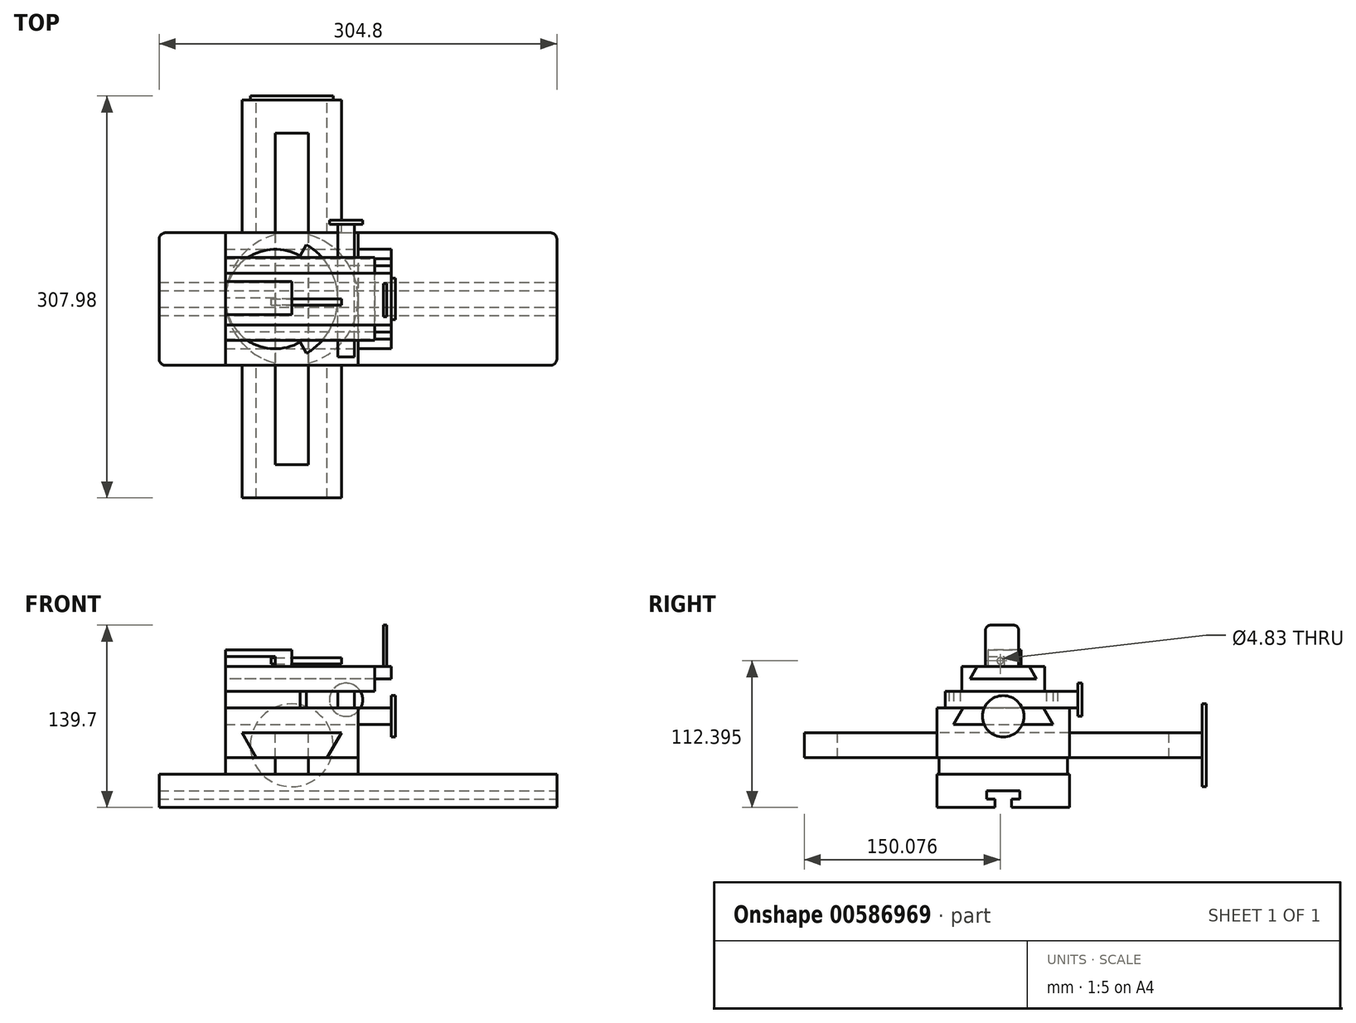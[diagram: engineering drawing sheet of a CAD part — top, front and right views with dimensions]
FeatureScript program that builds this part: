
annotation { "Feature Type Name" : "Feature", "Feature Type Description" : "" }
export const myFeature = defineFeature(function(context is Context, id is Id, definition is map)
    precondition{}
    {
        {
            var Q0;
            Q0=qCreatedBy(makeId("Top.planeOp"),FACE);
            var sketch = newSketch(context, id + "F0", { "sketchPlane" : qUnion([Q0])});
            skLineSegment(sketch, "E0.bottom", {"start": v(0, 0) * mm, "end": v(304.8, 0) * mm});
            skLineSegment(sketch, "E0.top", {"start": v(0, 101.6) * mm, "end": v(304.8, 101.6) * mm});
            skLineSegment(sketch, "E0.left", {"start": v(0, 0) * mm, "end": v(0, 101.6) * mm});
            skLineSegment(sketch, "E0.right", {"start": v(304.8, 0) * mm, "end": v(304.8, 101.6) * mm});
            skSolve(sketch);
        }
        {
            var Q0;
            Q0 = qSketchRegion(id + "F0", true);
            extrude(context, id + "F1", {"entities" : qUnion([Q0]), "depth" : 25.4 * mm, "offsetDistance" : 25.4 * mm});
        }
        {
            var Q0;
            Q0=makeQuery(id+"F1.opExtrude","SWEPT_EDGE",EDGE,{"disambiguationData":[OSD([sQuery(id+"F0.wireOp",EDGE,"E0.bottom"),sQuery(id+"F0.wireOp",EDGE,"E0.left")])]});
            var Q1;
            Q1=makeQuery(id+"F1.opExtrude","SWEPT_EDGE",EDGE,{"disambiguationData":[OSD([sQuery(id+"F0.wireOp",EDGE,"E0.bottom"),sQuery(id+"F0.wireOp",EDGE,"E0.right")])]});
            var Q2;
            Q2=makeQuery(id+"F1.opExtrude","SWEPT_EDGE",EDGE,{"disambiguationData":[OSD([sQuery(id+"F0.wireOp",EDGE,"E0.top"),sQuery(id+"F0.wireOp",EDGE,"E0.right")])]});
            var Q3;
            Q3=makeQuery(id+"F1.opExtrude","SWEPT_EDGE",EDGE,{"disambiguationData":[OSD([sQuery(id+"F0.wireOp",EDGE,"E0.top"),sQuery(id+"F0.wireOp",EDGE,"E0.left")])]});
            fillet(context, id + "F2", {"entities" : qUnion([Q0, Q1, Q2, Q3]), "radius" : 5.08 * mm, "tangentPropagation" : true, "allowEdgeOverflow" : false});
        }
        {
            var Q0;
            Q0=makeQuery(id+"F1.opExtrude","SWEPT_FACE",FACE,{"disambiguationData":[OSD([sQuery(id+"F0.wireOp",EDGE,"E0.right")])]});
            var sketch = newSketch(context, id + "F3", { "sketchPlane" : qUnion([Q0])});
            skLineSegment(sketch, "E1", {"start": v(44.45, 0) * mm, "end": v(44.45, 6.35) * mm});
            skLineSegment(sketch, "E2", {"start": v(44.45, 6.35) * mm, "end": v(38.1, 6.35) * mm});
            skLineSegment(sketch, "E3", {"start": v(38.1, 6.35) * mm, "end": v(38.1, 12.7) * mm});
            skLineSegment(sketch, "E4", {"start": v(38.1, 12.7) * mm, "end": v(63.5, 12.7) * mm});
            skLineSegment(sketch, "E5", {"start": v(63.5, 12.7) * mm, "end": v(63.5, 6.35) * mm});
            skLineSegment(sketch, "E6", {"start": v(63.5, 6.35) * mm, "end": v(57.15, 6.35) * mm});
            skLineSegment(sketch, "E7", {"start": v(57.15, 6.35) * mm, "end": v(57.15, 0) * mm});
            skLineSegment(sketch, "E8", {"start": v(57.15, 0) * mm, "end": v(44.45, 0) * mm});
            skSolve(sketch);
        }
        {
            var Q0;
            Q0 = qSketchRegion(id + "F3", true);
            extrude(context, id + "F4", {"entities" : qUnion([Q0]), "operationType" : NewBodyOperationType.REMOVE, "endBound" : BoundingType.THROUGH_ALL, "oppositeDirection" : true, "depth" : 25.4 * mm, "offsetDistance" : 25.4 * mm});
        }
        {
            var Q0;
            Q0=makeQuery(id+"F1.opExtrude","CAP_FACE",FACE,{"disambiguationData":[OSD([sQuery(id+"F0.wireOp",EDGE,"E0.bottom"),sQuery(id+"F0.wireOp",EDGE,"E0.top"),sQuery(id+"F0.wireOp",EDGE,"E0.left"),sQuery(id+"F0.wireOp",EDGE,"E0.right")])],"isStart":false});
            var sketch = newSketch(context, id + "F5", { "sketchPlane" : qUnion([Q0])});
            skCircle(sketch, "E9", {"center": v(101.6, 50.8) * mm, "radius": 50.8 * mm});
            skSolve(sketch);
        }
        {
            var Q0;
            {var subQ0=sQuery(id+"F5.wireOp",EDGE,"E9");var subQ1=makeQuery(id+"F5.imprint","INTERSECT",VERTEX,{"derivedFrom":[makeQuery(id+"F1.opExtrude","CAP_EDGE",EDGE,{"disambiguationData":[OSD([sQuery(id+"F0.wireOp",EDGE,"E0.bottom")])],"isStart":false}),subQ0]});Q0=makeQuery(id+"F5.imprint","IMPRINT",FACE,{"disambiguationData":[TD([[makeQuery(id+"F5.imprint","IMPRINT",EDGE,{"disambiguationData":[TD([[subQ1,1.0]])],"derivedFrom":subQ0}),1.0]])]});}
            extrude(context, id + "F6", {"entities" : qUnion([Q0]), "depth" : 12.7 * mm, "offsetDistance" : 25.4 * mm});
        }
        {
            var Q0;
            Q0=makeQuery(id+"F6.opExtrude","CAP_FACE",FACE,{"disambiguationData":[OSD([sQuery(id+"F5.wireOp",EDGE,"E9")])],"isStart":false});
            var sketch = newSketch(context, id + "F7", { "sketchPlane" : qUnion([Q0])});
            skLineSegment(sketch, "E10.bottom", {"start": v(50.8, 101.6) * mm, "end": v(152.4, 101.6) * mm});
            skLineSegment(sketch, "E10.top", {"start": v(50.8, 0) * mm, "end": v(152.4, 0) * mm});
            skLineSegment(sketch, "E10.left", {"start": v(50.8, 101.6) * mm, "end": v(50.8, 0) * mm});
            skLineSegment(sketch, "E10.right", {"start": v(152.4, 101.6) * mm, "end": v(152.4, 0) * mm});
            skSolve(sketch);
        }
        {
            var Q0;
            Q0 = qSketchRegion(id + "F7", true);
            extrude(context, id + "F8", {"entities" : qUnion([Q0]), "depth" : 38.1 * mm, "offsetDistance" : 25.4 * mm});
        }
        {
            var Q0;
            Q0=makeQuery(id+"F8.opExtrude","SWEPT_FACE",FACE,{"disambiguationData":[OSD([sQuery(id+"F7.wireOp",EDGE,"E10.top")])]});
            var sketch = newSketch(context, id + "F9", { "sketchPlane" : qUnion([Q0])});
            skLineSegment(sketch, "E11", {"start": v(74.5, 38.1) * mm, "end": v(63.5, 57.15) * mm});
            skLineSegment(sketch, "E12", {"start": v(63.5, 57.15) * mm, "end": v(139.7, 57.15) * mm});
            skLineSegment(sketch, "E13", {"start": v(139.7, 57.15) * mm, "end": v(128.7, 38.1) * mm});
            skLineSegment(sketch, "E14", {"start": v(74.5, 38.1) * mm, "end": v(128.7, 38.1) * mm});
            skSolve(sketch);
        }
        {
            var Q0;
            Q0 = qSketchRegion(id + "F9", true);
            extrude(context, id + "F10", {"entities" : qUnion([Q0]), "operationType" : NewBodyOperationType.REMOVE, "endBound" : BoundingType.UP_TO_NEXT, "oppositeDirection" : true, "depth" : 25.4 * mm, "offsetDistance" : 25.4 * mm});
        }
        {
            var Q0;
            Q0=makeQuery(id+"F8.opExtrude","SWEPT_FACE",FACE,{"disambiguationData":[OSD([sQuery(id+"F7.wireOp",EDGE,"E10.right")])]});
            var sketch = newSketch(context, id + "F11", { "sketchPlane" : qUnion([Q0])});
            skLineSegment(sketch, "E15", {"start": v(20.03, 76.2) * mm, "end": v(12.7, 63.5) * mm});
            skLineSegment(sketch, "E16", {"start": v(12.7, 63.5) * mm, "end": v(88.9, 63.5) * mm});
            skLineSegment(sketch, "E17", {"start": v(88.9, 63.5) * mm, "end": v(81.57, 76.2) * mm});
            skLineSegment(sketch, "E18", {"start": v(20.03, 76.2) * mm, "end": v(81.57, 76.2) * mm});
            skSolve(sketch);
        }
        {
            var Q0;
            Q0 = qSketchRegion(id + "F11", true);
            extrude(context, id + "F12", {"entities" : qUnion([Q0]), "operationType" : NewBodyOperationType.REMOVE, "endBound" : BoundingType.UP_TO_NEXT, "oppositeDirection" : true, "depth" : 25.4 * mm, "offsetDistance" : 25.4 * mm});
        }
        {
            var Q0;
            Q0 = qSketchRegion(id + "F9", true);
            extrude(context, id + "F13", {"entities" : qUnion([Q0]), "depth" : 101.6 * mm, "offsetDistance" : 25.4 * mm});
        }
        {
            var Q0;
            Q0 = qSketchRegion(id + "F9", true);
            extrude(context, id + "F14", {"entities" : qUnion([Q0]), "operationType" : NewBodyOperationType.ADD, "oppositeDirection" : true, "depth" : 203.2 * mm, "offsetDistance" : 25.4 * mm});
        }
        {
            var Q0;
            {var subQ0=sQuery(id+"F9.wireOp",EDGE,"E12");Q0=makeQuery(id+"F14.boolean.opBoolean","MERGE",FACE,{"derivedFrom":[makeQuery(id+"F13.opExtrude","SWEPT_FACE",FACE,{"disambiguationData":[OSD([subQ0])]}),makeQuery(id+"F14.opExtrude","SWEPT_FACE",FACE,{"disambiguationData":[OSD([subQ0])]})]});}
            var sketch = newSketch(context, id + "F15", { "sketchPlane" : qUnion([Q0])});
            skLineSegment(sketch, "E19.bottom", {"start": v(88.9, 177.8) * mm, "end": v(114.3, 177.8) * mm});
            skLineSegment(sketch, "E19.top", {"start": v(88.9, -76.2) * mm, "end": v(114.3, -76.2) * mm});
            skLineSegment(sketch, "E19.left", {"start": v(88.9, 177.8) * mm, "end": v(88.9, -76.2) * mm});
            skLineSegment(sketch, "E19.right", {"start": v(114.3, 177.8) * mm, "end": v(114.3, -76.2) * mm});
            skSolve(sketch);
        }
        {
            var Q0;
            Q0 = qSketchRegion(id + "F15", true);
            extrude(context, id + "F16", {"entities" : qUnion([Q0]), "operationType" : NewBodyOperationType.REMOVE, "endBound" : BoundingType.UP_TO_NEXT, "oppositeDirection" : true, "depth" : 25.4 * mm, "offsetDistance" : 25.4 * mm});
        }
        {
            var Q0;
            Q0=makeQuery(id+"F14.opExtrude","CAP_FACE",FACE,{"disambiguationData":[OSD([sQuery(id+"F9.wireOp",EDGE,"E11"),sQuery(id+"F9.wireOp",EDGE,"E12"),sQuery(id+"F9.wireOp",EDGE,"E13"),sQuery(id+"F9.wireOp",EDGE,"E14")])],"isStart":false});
            var sketch = newSketch(context, id + "F17", { "sketchPlane" : qUnion([Q0])});
            skCircle(sketch, "E20", {"center": v(-101.6, 47.63) * mm, "radius": 31.75 * mm});
            skSolve(sketch);
        }
        {
            var Q0;
            Q0 = qSketchRegion(id + "F17", true);
            extrude(context, id + "F18", {"entities" : qUnion([Q0]), "depth" : 3.17 * mm, "offsetDistance" : 25.4 * mm});
        }
        {
            var Q0;
            Q0 = qSketchRegion(id + "F11", true);
            extrude(context, id + "F19", {"entities" : qUnion([Q0]), "oppositeDirection" : true, "depth" : 101.6 * mm, "offsetDistance" : 25.4 * mm, "hasSecondDirection" : true, "secondDirectionOppositeDirection" : false, "secondDirectionDepth" : 25.4 * mm});
        }
        {
            var Q0;
            Q0=makeQuery(id+"F19.opExtrude","CAP_FACE",FACE,{"disambiguationData":[OSD([sQuery(id+"F11.wireOp",EDGE,"E15"),sQuery(id+"F11.wireOp",EDGE,"E16"),sQuery(id+"F11.wireOp",EDGE,"E17"),sQuery(id+"F11.wireOp",EDGE,"E18")])],"isStart":true});
            var sketch = newSketch(context, id + "F20", { "sketchPlane" : qUnion([Q0])});
            skCircle(sketch, "E21", {"center": v(50.8, 69.85) * mm, "radius": 15.88 * mm});
            skSolve(sketch);
        }
        {
            var Q0;
            Q0 = qSketchRegion(id + "F20", true);
            extrude(context, id + "F21", {"entities" : qUnion([Q0]), "depth" : 3.17 * mm, "offsetDistance" : 25.4 * mm});
        }
        {
            var Q0;
            Q0=makeQuery(id+"F19.opExtrude","SWEPT_FACE",FACE,{"disambiguationData":[OSD([sQuery(id+"F11.wireOp",EDGE,"E18")])]});
            var sketch = newSketch(context, id + "F22", { "sketchPlane" : qUnion([Q0])});
            skArc(sketch, "E22", {"start": v(107.95, 83.8) * mm, "mid": v(50.8, 50.8) * mm, "end": v(107.95, 17.8) * mm});
            skLineSegment(sketch, "E23", {"start": v(107.95, 17.8) * mm, "end": v(112.9, 9.24) * mm});
            skLineSegment(sketch, "E24", {"start": v(107.95, 83.8) * mm, "end": v(112.9, 92.36) * mm});
            skArc(sketch, "E25", {"start": v(112.9, 9.24) * mm, "mid": v(136.89, 50.8) * mm, "end": v(112.9, 92.36) * mm});
            skSolve(sketch);
        }
        {
            var Q0;
            Q0 = qSketchRegion(id + "F22", true);
            extrude(context, id + "F23", {"entities" : qUnion([Q0]), "depth" : 12.7 * mm, "offsetDistance" : 25.4 * mm});
        }
        {
            var Q0;
            Q0=makeQuery(id+"F19.opExtrude","SWEPT_FACE",FACE,{"disambiguationData":[OSD([sQuery(id+"F11.wireOp",EDGE,"E18")])]});
            var sketch = newSketch(context, id + "F24", { "sketchPlane" : qUnion([Q0])});
            skLineSegment(sketch, "E26.bottom", {"start": v(136.89, 6.35) * mm, "end": v(149.59, 6.35) * mm});
            skLineSegment(sketch, "E26.top", {"start": v(136.89, 107.95) * mm, "end": v(149.59, 107.95) * mm});
            skLineSegment(sketch, "E26.left", {"start": v(136.89, 6.35) * mm, "end": v(136.89, 107.95) * mm});
            skLineSegment(sketch, "E26.right", {"start": v(149.59, 6.35) * mm, "end": v(149.59, 107.95) * mm});
            skSolve(sketch);
        }
        {
            var Q0;
            Q0 = qSketchRegion(id + "F24", true);
            extrude(context, id + "F25", {"entities" : qUnion([Q0]), "depth" : 12.7 * mm, "offsetDistance" : 25.4 * mm});
        }
        {
            var Q0;
            Q0=makeQuery(id+"F25.opExtrude","SWEPT_FACE",FACE,{"disambiguationData":[OSD([sQuery(id+"F24.wireOp",EDGE,"E26.top")])]});
            var sketch = newSketch(context, id + "F26", { "sketchPlane" : qUnion([Q0])});
            skCircle(sketch, "E27", {"center": v(-143.24, 82.55) * mm, "radius": 12.7 * mm});
            skSolve(sketch);
        }
        {
            var Q0;
            Q0 = qSketchRegion(id + "F26", true);
            extrude(context, id + "F27", {"entities" : qUnion([Q0]), "depth" : 3.17 * mm, "offsetDistance" : 25.4 * mm});
        }
        {
            var Q0;
            Q0=makeQuery(id+"F23.opExtrude","CAP_FACE",FACE,{"disambiguationData":[OSD([sQuery(id+"F22.wireOp",EDGE,"E22"),sQuery(id+"F22.wireOp",EDGE,"E23"),sQuery(id+"F22.wireOp",EDGE,"E24"),sQuery(id+"F22.wireOp",EDGE,"E25")])],"isStart":false});
            var sketch = newSketch(context, id + "F28", { "sketchPlane" : qUnion([Q0])});
            skLineSegment(sketch, "E28.bottom", {"start": v(50.8, 19.05) * mm, "end": v(165.1, 19.05) * mm});
            skLineSegment(sketch, "E28.top", {"start": v(50.8, 82.55) * mm, "end": v(165.1, 82.55) * mm});
            skLineSegment(sketch, "E28.left", {"start": v(50.8, 19.05) * mm, "end": v(50.8, 82.55) * mm});
            skLineSegment(sketch, "E28.right", {"start": v(165.1, 19.05) * mm, "end": v(165.1, 82.55) * mm});
            skSolve(sketch);
        }
        {
            var Q0;
            Q0 = qSketchRegion(id + "F28", true);
            extrude(context, id + "F29", {"entities" : qUnion([Q0]), "depth" : 19.05 * mm, "offsetDistance" : 25.4 * mm});
        }
        {
            var Q0;
            Q0=makeQuery(id+"F29.opExtrude","SWEPT_FACE",FACE,{"disambiguationData":[OSD([sQuery(id+"F28.wireOp",EDGE,"E28.left")])]});
            var sketch = newSketch(context, id + "F30", { "sketchPlane" : qUnion([Q0])});
            skLineSegment(sketch, "E29", {"start": v(-70.7, 107.95) * mm, "end": v(-30.9, 107.95) * mm});
            skLineSegment(sketch, "E30", {"start": v(-30.9, 107.95) * mm, "end": v(-25.4, 98.42) * mm});
            skLineSegment(sketch, "E31", {"start": v(-25.4, 98.42) * mm, "end": v(-76.2, 98.42) * mm});
            skLineSegment(sketch, "E32", {"start": v(-76.2, 98.42) * mm, "end": v(-70.7, 107.95) * mm});
            skSolve(sketch);
        }
        {
            var Q0;
            Q0 = qSketchRegion(id + "F30", true);
            extrude(context, id + "F31", {"entities" : qUnion([Q0]), "operationType" : NewBodyOperationType.REMOVE, "endBound" : BoundingType.UP_TO_NEXT, "oppositeDirection" : true, "depth" : 25.4 * mm, "offsetDistance" : 25.4 * mm});
        }
        {
            var Q0;
            Q0 = qSketchRegion(id + "F30", true);
            extrude(context, id + "F32", {"entities" : qUnion([Q0]), "oppositeDirection" : true, "depth" : 127 * mm, "offsetDistance" : 25.4 * mm});
        }
        {
            var Q0;
            Q0=makeQuery(id+"F32.opExtrude","SWEPT_FACE",FACE,{"disambiguationData":[OSD([sQuery(id+"F30.wireOp",EDGE,"E29")])]});
            var sketch = newSketch(context, id + "F33", { "sketchPlane" : qUnion([Q0])});
            skLineSegment(sketch, "E33.bottom", {"start": v(50.8, 64.35) * mm, "end": v(101.6, 64.35) * mm});
            skLineSegment(sketch, "E33.top", {"start": v(50.8, 38.95) * mm, "end": v(101.6, 38.95) * mm});
            skLineSegment(sketch, "E33.left", {"start": v(50.8, 64.35) * mm, "end": v(50.8, 38.95) * mm});
            skLineSegment(sketch, "E33.right", {"start": v(101.6, 64.35) * mm, "end": v(101.6, 38.95) * mm});
            skSolve(sketch);
        }
        {
            var Q0;
            Q0 = qSketchRegion(id + "F33", true);
            extrude(context, id + "F34", {"entities" : qUnion([Q0]), "depth" : 12.7 * mm, "offsetDistance" : 25.4 * mm});
        }
        {
            var Q0;
            Q0=makeQuery(id+"F34.opExtrude","SWEPT_FACE",FACE,{"disambiguationData":[OSD([sQuery(id+"F33.wireOp",EDGE,"E33.left")])]});
            var sketch = newSketch(context, id + "F35", { "sketchPlane" : qUnion([Q0])});
            skLineSegment(sketch, "E34.bottom", {"start": v(-38.95, 107.95) * mm, "end": v(-51.65, 107.95) * mm});
            skLineSegment(sketch, "E34.top", {"start": v(-38.95, 115.57) * mm, "end": v(-51.65, 115.57) * mm});
            skLineSegment(sketch, "E34.left", {"start": v(-38.95, 107.95) * mm, "end": v(-38.95, 115.57) * mm});
            skLineSegment(sketch, "E34.right", {"start": v(-51.65, 107.95) * mm, "end": v(-51.65, 115.57) * mm});
            skSolve(sketch);
        }
        {
            var Q0;
            Q0 = qSketchRegion(id + "F35", true);
            extrude(context, id + "F36", {"entities" : qUnion([Q0]), "operationType" : NewBodyOperationType.REMOVE, "oppositeDirection" : true, "depth" : 38.1 * mm, "offsetDistance" : 25.4 * mm});
        }
        {
            var Q0;
            Q0=makeQuery(id+"F36.boolean.opBoolean","COPY",FACE,{"derivedFrom":makeQuery(id+"F36.opExtrude","CAP_FACE",FACE,{"disambiguationData":[OSD([sQuery(id+"F35.wireOp",EDGE,"E34.bottom"),sQuery(id+"F35.wireOp",EDGE,"E34.top"),sQuery(id+"F35.wireOp",EDGE,"E34.left"),sQuery(id+"F35.wireOp",EDGE,"E34.right")])],"isStart":false})});
            var sketch = newSketch(context, id + "F37", { "sketchPlane" : qUnion([Q0])});
            skCircle(sketch, "E35", {"center": v(-48.48, 112.4) * mm, "radius": 2.41 * mm});
            skSolve(sketch);
        }
        {
            var Q0;
            Q0 = qSketchRegion(id + "F37", true);
            extrude(context, id + "F38", {"entities" : qUnion([Q0]), "operationType" : NewBodyOperationType.REMOVE, "endBound" : BoundingType.UP_TO_NEXT, "oppositeDirection" : true, "depth" : 25.4 * mm, "offsetDistance" : 25.4 * mm});
        }
        {
            var Q0;
            Q0 = qSketchRegion(id + "F37", true);
            extrude(context, id + "F39", {"entities" : qUnion([Q0]), "depth" : 3.17 * mm, "offsetDistance" : 25.4 * mm, "hasSecondDirection" : true, "secondDirectionOppositeDirection" : true, "secondDirectionDepth" : 50.8 * mm});
        }
        {
            var Q0;
            Q0=makeQuery(id+"F32.opExtrude","SWEPT_FACE",FACE,{"disambiguationData":[OSD([sQuery(id+"F30.wireOp",EDGE,"E29")])]});
            var sketch = newSketch(context, id + "F40", { "sketchPlane" : qUnion([Q0])});
            skLineSegment(sketch, "E36.bottom", {"start": v(171.92, 37.25) * mm, "end": v(174.3, 37.25) * mm});
            skLineSegment(sketch, "E36.top", {"start": v(171.92, 62.65) * mm, "end": v(174.3, 62.65) * mm});
            skLineSegment(sketch, "E36.left", {"start": v(171.92, 37.25) * mm, "end": v(171.92, 62.65) * mm});
            skLineSegment(sketch, "E36.right", {"start": v(174.3, 37.25) * mm, "end": v(174.3, 62.65) * mm});
            skSolve(sketch);
        }
        {
            var Q0;
            Q0 = qSketchRegion(id + "F40", true);
            extrude(context, id + "F41", {"entities" : qUnion([Q0]), "depth" : 31.75 * mm, "offsetDistance" : 25.4 * mm});
        }
        {
            var Q0;
            Q0=makeQuery(id+"F41.opExtrude","CAP_EDGE",EDGE,{"disambiguationData":[OSD([sQuery(id+"F40.wireOp",EDGE,"E36.bottom")])],"isStart":false});
            var Q1;
            Q1=makeQuery(id+"F41.opExtrude","CAP_EDGE",EDGE,{"disambiguationData":[OSD([sQuery(id+"F40.wireOp",EDGE,"E36.top")])],"isStart":false});
            fillet(context, id + "F42", {"entities" : qUnion([Q0, Q1]), "radius" : 3.8 * mm, "tangentPropagation" : true, "allowEdgeOverflow" : false});
        }
    });
